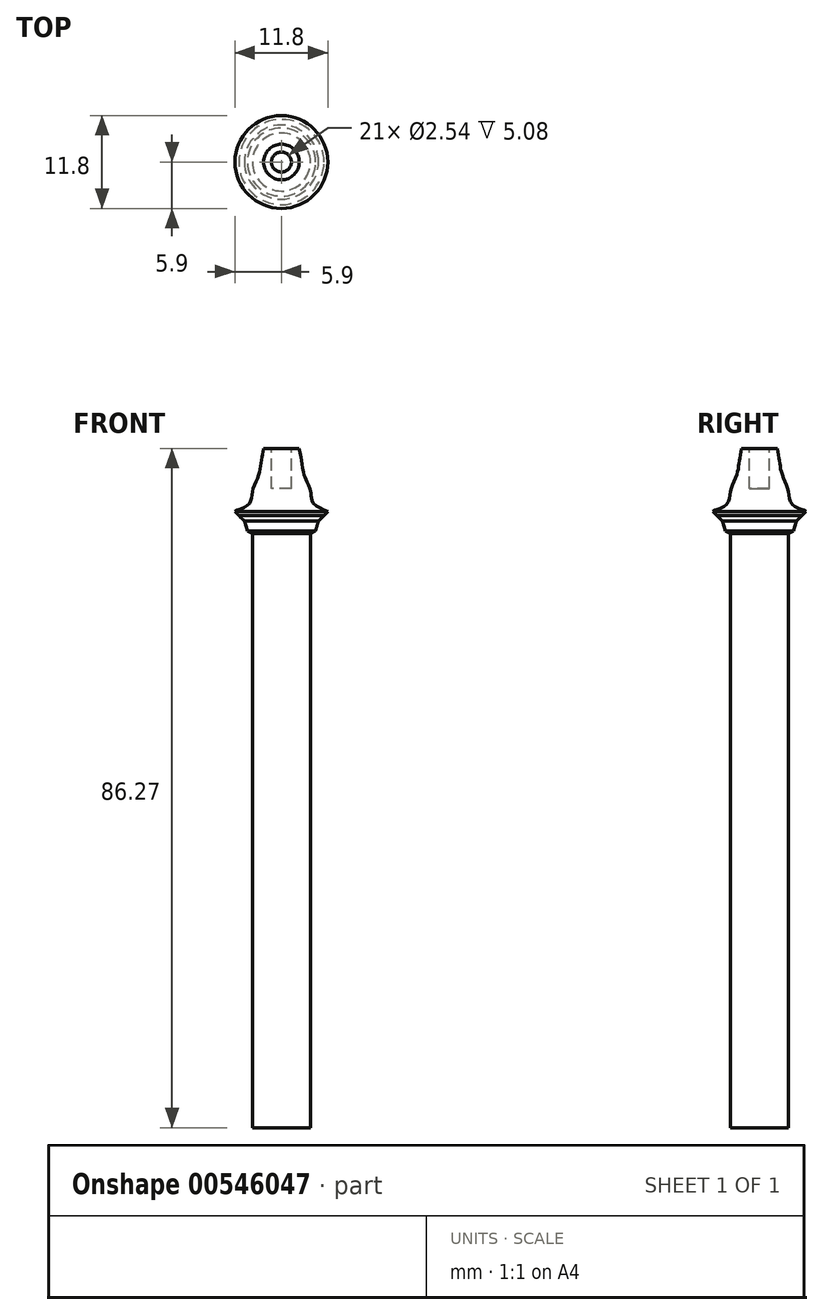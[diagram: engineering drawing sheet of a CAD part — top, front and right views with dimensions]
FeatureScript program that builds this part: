
annotation { "Feature Type Name" : "Feature", "Feature Type Description" : "" }
export const myFeature = defineFeature(function(context is Context, id is Id, definition is map)
    precondition{}
    {
        {
            var Q0;
            Q0=qCreatedBy(makeId("Front.planeOp"),FACE);
            var sketch = newSketch(context, id + "F0", { "sketchPlane" : qUnion([Q0])});
            skLineSegment(sketch, "E0", {"start": v(0, 0) * mm, "end": v(0, 76.2) * mm});
            skLineSegment(sketch, "E1", {"start": v(0, 0) * mm, "end": v(3.68, 0) * mm});
            skLineSegment(sketch, "E2", {"start": v(3.68, 0) * mm, "end": v(3.68, 50.59) * mm});
            skLineSegment(sketch, "E3", {"start": v(3.68, 50.59) * mm, "end": v(3.68, 75.47) * mm});
            skFitSpline(sketch, "E4", {"points": [v(3.68, 75.47) * mm, v(5.47, 76.46) * mm, v(6.83, 76.96) * mm, v(8.48, 77.1) * mm, v(6.66, 77.77) * mm, v(5.9, 78.28) * mm, v(4.12, 79.25) * mm, v(3.68, 80.85) * mm, v(2.85, 83.05) * mm, v(2.56, 84.7) * mm, v(2.26, 86.27) * mm], "startDerivative": vector(17.7, 9.68) * mm, "endDerivative": vector(-3.48, 16.24) * mm});
            skLineSegment(sketch, "E5", {"start": v(0, 76.2) * mm, "end": v(0, 86.52) * mm});
            skLineSegment(sketch, "E6", {"start": v(0, 85.74) * mm, "end": v(-0.12, 86.27) * mm});
            skLineSegment(sketch, "E7", {"start": v(-0.12, 86.27) * mm, "end": v(2.26, 86.27) * mm});
            skLineSegment(sketch, "E8", {"start": v(4.33, 75.82) * mm, "end": v(4.7, 77.08) * mm});
            skLineSegment(sketch, "E9", {"start": v(4.7, 77.08) * mm, "end": v(5.4, 77.74) * mm});
            skLineSegment(sketch, "E10", {"start": v(5.4, 77.74) * mm, "end": v(5.9, 78.28) * mm});
            skSolve(sketch);
        }
        {
            var Q0;
            Q0=makeQuery(id+"F0.imprint","IMPRINT",FACE,{"disambiguationData":[TD([[makeQuery(id+"F0.imprint","IMPRINT",EDGE,{"derivedFrom":sQuery(id+"F0.wireOp",EDGE,"7WPgAVXb-QW13-Q4uv-7ZYp-fjhG4gKAQ60v")}),-1.0]])]});
            var Q1;
            Q1=makeQuery(id+"F0.imprint","IMPRINT",FACE,{"disambiguationData":[TD([[makeQuery(id+"F0.imprint","IMPRINT",EDGE,{"derivedFrom":sQuery(id+"F0.wireOp",EDGE,"f21zjGco-0Yui-h6FH-L9na-skuH6J8rJ9y1")}),-1.0]])]});
            var Q2;
            Q2=makeQuery(id+"F0.imprint","IMPRINT",FACE,{"disambiguationData":[TD([[makeQuery(id+"F0.imprint","IMPRINT",EDGE,{"derivedFrom":sQuery(id+"F0.wireOp",EDGE,"E0")}),-1.0]])]});
            var Q3;
            Q3=sQuery(id+"F0.wireOp",EDGE,"E0");
            revolve(context, id + "F1", {"entities" : qUnion([Q0, Q1, Q2]), "axis" : qUnion([Q3]), "revolveType" : RevolveType.FULL});
        }
        {
            var Q0;
            Q0=makeQuery(id+"F1.opRevolve","SWEPT_FACE",FACE,{"disambiguationData":[OSD([sQuery(id+"F0.wireOp",EDGE,"E7")])]});
            var sketch = newSketch(context, id + "F2", { "sketchPlane" : qUnion([Q0])});
            skCircle(sketch, "E11", {"center": v(0, 0) * mm, "radius": 1.27 * mm});
            skSolve(sketch);
        }
        {
            var Q0;
            Q0 = qSketchRegion(id + "F2", true);
            extrude(context, id + "F3", {"entities" : qUnion([Q0]), "operationType" : NewBodyOperationType.REMOVE, "oppositeDirection" : true, "depth" : 5.08 * mm, "offsetDistance" : 25.4 * mm});
        }
    });
